# Revit family: Loading Docks_Shelter_Ultigroup_Rollout Container - PVC 3000 mm
name_source: partatom
category: Generic Models
units: mm (PartAtom-declared; Revit-internal decimal feet)

## family parameters
Always vertical = Yes
Can host rebar = No
Cut with Voids When Loaded = No
OmniClass Number = 23.50.70.24
OmniClass Title = Seals and Shelters
Part Type = Normal
Room Calculation Point = No
Round Connector Dimension = Use Diameter
Shared = No
Work Plane-Based = No

## types (2) — shared parameters
Bottom Joins = 345 mm
Connector Material = Connector Material
Description = Rollout Container Shelter 3000 mm
Dock Curtain = Yes
Dock Shelter Curtain = Curtain Material
Dock Shelter Front Flaps = Front Flaps Material
Dock Shelter Overall Height = 3525 mm  [stored 11.565 ft]
Fax = 07 846 2467
Manufacturer = Ulti Group Ltd.
Model = Ulti Rollout Container Shelter - PVC 3000 mm
Rail Length = 3000 mm  [stored 9.84252 ft]
Send Message = http://ultigroup.co.nz
Steel Rail = Steel Rail
Top Joins = 1400 mm  [stored 4.59318 ft]
URL = www.ultigroup.co.nz
zero-valued in all types: Default Elevation, InstallationGroup_ANZRS, ModifiedIssue_ANZRS

## per-type parameters (varying)
| type | Dock Shelter Overall Depth | Dock Shelter Overall Width | Shelter Top Flap | Side Flaps Wdth |
| Type 1 | 3000 mm  [stored 9.84252 ft] | 4500 mm | 1000 mm  [stored 3.28084 ft] | 1200 mm |
| Type 2 | 650 mm | 3500 mm  [stored 11.4829 ft] | 945 mm | 575 mm |

note: [stored X ft] marks values corroborated as IEEE doubles in the binary element streams (Revit-internal decimal feet)

## geometry (parser evidence)
native form markers: Blend x2, Sweep x19
no freeform markers — native parametric forms only
